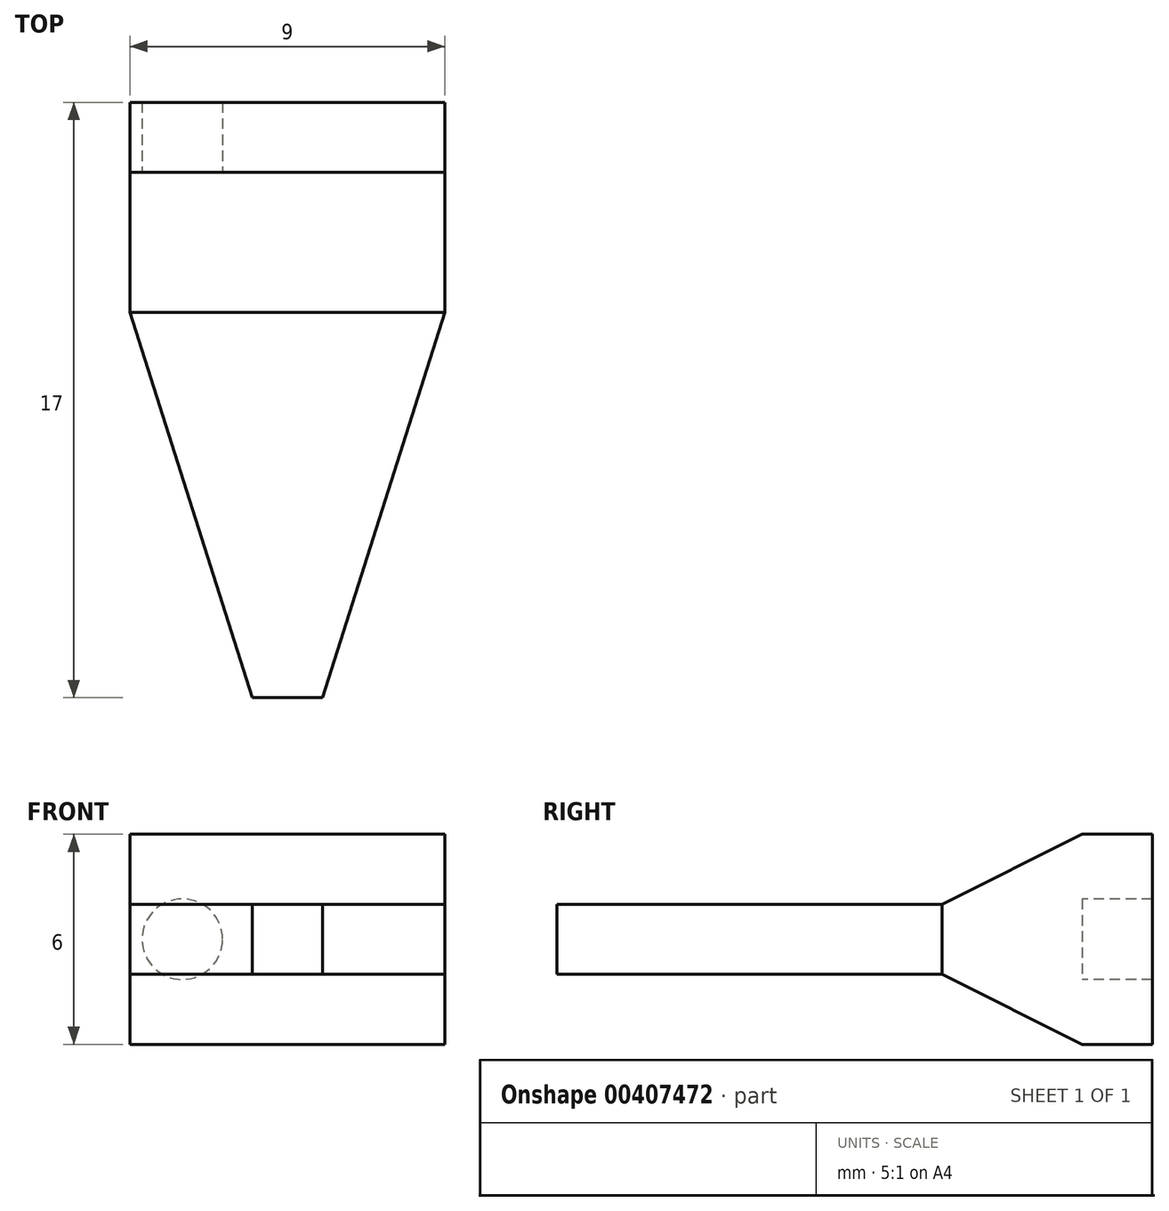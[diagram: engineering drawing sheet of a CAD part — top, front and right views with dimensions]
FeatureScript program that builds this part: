
annotation { "Feature Type Name" : "Feature", "Feature Type Description" : "" }
export const myFeature = defineFeature(function(context is Context, id is Id, definition is map)
    precondition{}
    {
        {
            var Q0;
            Q0=qCreatedBy(makeId("Top.planeOp"),FACE);
            var sketch = newSketch(context, id + "F0", { "sketchPlane" : qUnion([Q0])});
            skLineSegment(sketch, "E0.bottom", {"start": v(4.5, 7.5) * mm, "end": v(-4.5, 7.5) * mm});
            skLineSegment(sketch, "E0.top", {"start": v(1, -7.5) * mm, "end": v(-1, -7.5) * mm});
            skLineSegment(sketch, "E0.left", {"start": v(4.5, 7.5) * mm, "end": v(4.5, 3.5) * mm});
            skLineSegment(sketch, "E0.right", {"start": v(-4.5, 7.5) * mm, "end": v(-4.5, 3.5) * mm});
            skPoint(sketch, "E0.middle", {"position": v(0, 0) * mm});
            skLineSegment(sketch, "E1", {"start": v(-4.5, 3.5) * mm, "end": v(-1, -7.5) * mm});
            skPoint(sketch, "E2.orphan", {"position": v(-4.5, -7.5) * mm});
            skLineSegment(sketch, "E3.MirrorCS", {"start": v(4.5, 3.5) * mm, "end": v(1, -7.5) * mm});
            skPoint(sketch, "E4.orphan", {"position": v(4.5, -7.5) * mm});
            skLineSegment(sketch, "E5", {"start": v(-4.5, 3.5) * mm, "end": v(4.5, 3.5) * mm});
            skSolve(sketch);
        }
        {
            var Q0;
            Q0=makeQuery(id+"F0.imprint","IMPRINT",FACE,{"disambiguationData":[TD([[makeQuery(id+"F0.imprint","IMPRINT",EDGE,{"derivedFrom":sQuery(id+"F0.wireOp",EDGE,"E0.bottom")}),1.0]])]});
            var Q1;
            Q1=makeQuery(id+"F0.imprint","IMPRINT",FACE,{"disambiguationData":[TD([[makeQuery(id+"F0.imprint","IMPRINT",EDGE,{"derivedFrom":sQuery(id+"F0.wireOp",EDGE,"E0.top")}),-1.0]])]});
            extrude(context, id + "F1", {"entities" : qUnion([Q0, Q1]), "depth" : 2 * mm});
        }
        {
            var Q0;
            Q0=makeQuery(id+"F0.imprint","IMPRINT",FACE,{"disambiguationData":[TD([[makeQuery(id+"F0.imprint","IMPRINT",EDGE,{"derivedFrom":sQuery(id+"F0.wireOp",EDGE,"E0.bottom")}),1.0]])]});
            extrude(context, id + "F2", {"entities" : qUnion([Q0]), "operationType" : NewBodyOperationType.ADD, "depth" : 4 * mm, "hasSecondDirection" : true, "secondDirectionOppositeDirection" : true, "secondDirectionDepth" : 2 * mm});
        }
        {
            var Q0;
            Q0=makeQuery(id+"F2.opExtrude","CAP_EDGE",EDGE,{"disambiguationData":[OSD([sQuery(id+"F0.wireOp",EDGE,"E5")])],"isStart":true});
            chamfer(context, id + "F3", {"entities" : qUnion([Q0]), "chamferType" : ChamferType.TWO_OFFSETS, "width1" : 2 * mm, "oppositeDirection" : false, "width2" : 4 * mm, "tangentPropagation" : true});
        }
        {
            var Q0;
            Q0=makeQuery(id+"F2.opExtrude","CAP_EDGE",EDGE,{"disambiguationData":[OSD([sQuery(id+"F0.wireOp",EDGE,"E5")])],"isStart":false});
            chamfer(context, id + "F4", {"entities" : qUnion([Q0]), "chamferType" : ChamferType.TWO_OFFSETS, "width1" : 2 * mm, "oppositeDirection" : true, "width2" : 4 * mm, "tangentPropagation" : true});
        }
        {
            var Q0;
            {var subQ0=sQuery(id+"F0.wireOp",EDGE,"E0.bottom");Q0=makeQuery(id+"F2.boolean.opBoolean","MERGE",FACE,{"derivedFrom":[makeQuery(id+"F1.opExtrude","SWEPT_FACE",FACE,{"disambiguationData":[OSD([subQ0])]}),makeQuery(id+"F2.opExtrude","SWEPT_FACE",FACE,{"disambiguationData":[OSD([subQ0])]})]});}
            var sketch = newSketch(context, id + "F5", { "sketchPlane" : qUnion([Q0])});
            skCircle(sketch, "E6", {"center": v(-3, 1) * mm, "radius": 1.15 * mm});
            skCircle(sketch, "E7.MirrorC", {"center": v(3, 1) * mm, "radius": 1.15 * mm});
            skSolve(sketch);
        }
        {
            var Q0;
            Q0=makeQuery(id+"F5.imprint","IMPRINT",FACE,{"disambiguationData":[TD([[makeQuery(id+"F5.imprint","IMPRINT",EDGE,{"derivedFrom":sQuery(id+"F5.wireOp",EDGE,"E6")}),1.0]])]});
            var Q1;
            Q1=makeQuery(id+"F5.imprint","IMPRINT",FACE,{"disambiguationData":[TD([[makeQuery(id+"F5.imprint","IMPRINT",EDGE,{"derivedFrom":sQuery(id+"F5.wireOp",EDGE,"E7.MirrorC")}),-1.0]])]});
            extrude(context, id + "F6", {"entities" : qUnion([Q0, Q1]), "operationType" : NewBodyOperationType.ADD, "depth" : 2 * mm});
        }
    });
